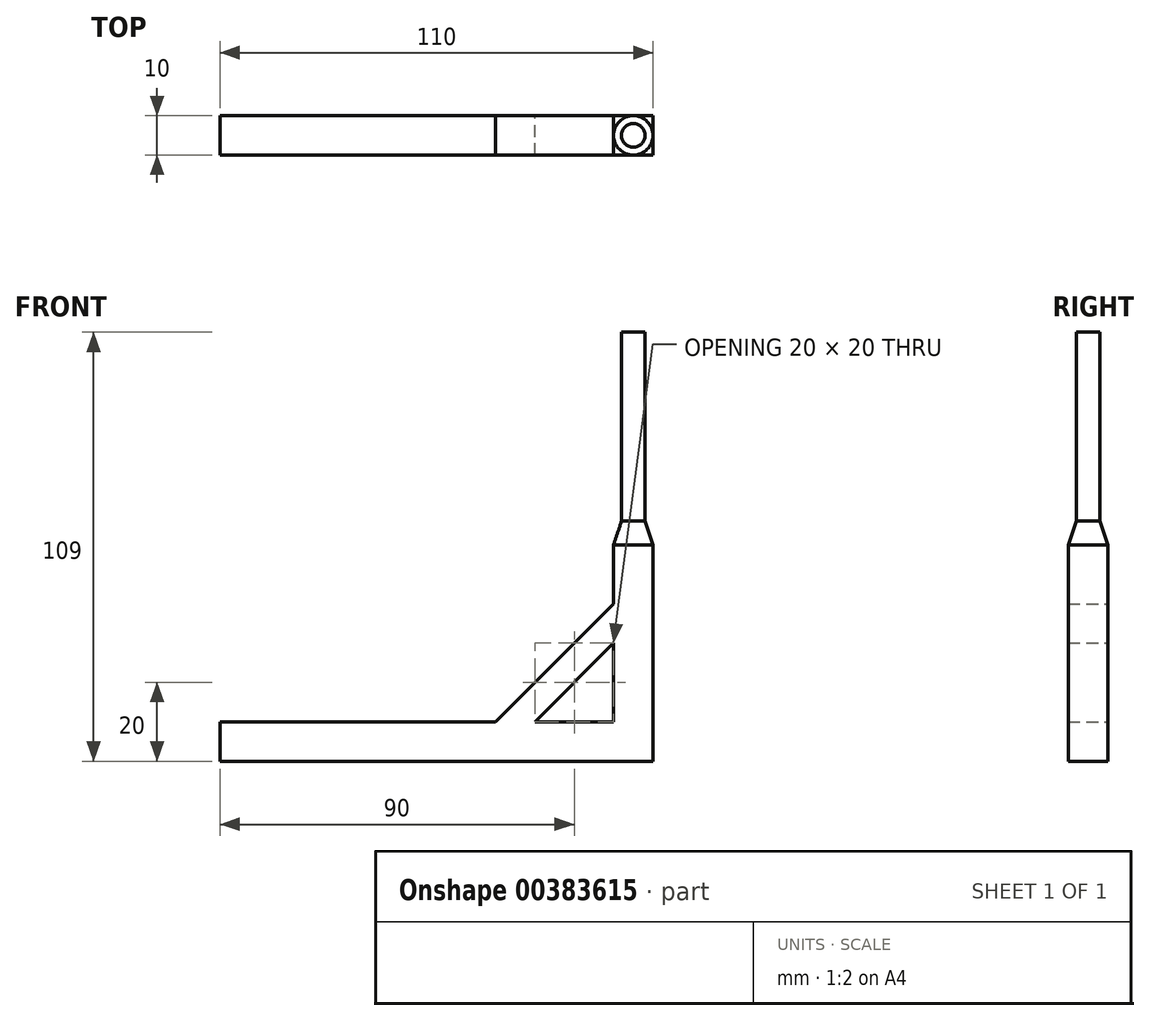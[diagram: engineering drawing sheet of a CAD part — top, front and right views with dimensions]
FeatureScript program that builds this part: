
annotation { "Feature Type Name" : "Feature", "Feature Type Description" : "" }
export const myFeature = defineFeature(function(context is Context, id is Id, definition is map)
    precondition{}
    {
        {
            var Q0;
            Q0=qCreatedBy(makeId("Top.planeOp"),FACE);
            var sketch = newSketch(context, id + "F0", { "sketchPlane" : qUnion([Q0])});
            skLineSegment(sketch, "E0.bottom", {"start": v(-55, 5) * mm, "end": v(55, 5) * mm});
            skLineSegment(sketch, "E0.top", {"start": v(-55, -5) * mm, "end": v(55, -5) * mm});
            skLineSegment(sketch, "E0.left", {"start": v(-55, 5) * mm, "end": v(-55, -5) * mm});
            skLineSegment(sketch, "E0.right", {"start": v(55, 5) * mm, "end": v(55, -5) * mm});
            skLineSegment(sketch, "E1", {"start": v(-55, 5) * mm, "end": v(55, -5) * mm, "construction": true});
            skLineSegment(sketch, "E2", {"start": v(55, 5) * mm, "end": v(-55, -5) * mm, "construction": true});
            skPoint(sketch, "E3", {"position": v(0, 0) * mm});
            skSolve(sketch);
        }
        {
            var Q0;
            Q0=makeQuery(id+"F0.imprint","IMPRINT",FACE,{"disambiguationData":[TD([[makeQuery(id+"F0.imprint","IMPRINT",EDGE,{"derivedFrom":sQuery(id+"F0.wireOp",EDGE,"E0.bottom")}),-1.0]])]});
            extrude(context, id + "F1", {"entities" : qUnion([Q0]), "depth" : 10 * mm});
        }
        {
            var Q0;
            Q0=makeQuery(id+"F1.opExtrude","CAP_FACE",FACE,{"disambiguationData":[OSD([sQuery(id+"F0.wireOp",EDGE,"E0.bottom"),sQuery(id+"F0.wireOp",EDGE,"E0.top"),sQuery(id+"F0.wireOp",EDGE,"E0.left"),sQuery(id+"F0.wireOp",EDGE,"E0.right")])],"isStart":false});
            var sketch = newSketch(context, id + "F2", { "sketchPlane" : qUnion([Q0])});
            skLineSegment(sketch, "E4.0", {"start": v(45, 5) * mm, "end": v(55, 5) * mm});
            skLineSegment(sketch, "E5.0", {"start": v(45, -5) * mm, "end": v(55, -5) * mm});
            skLineSegment(sketch, "E6.0", {"start": v(55, 5) * mm, "end": v(55, -5) * mm});
            skLineSegment(sketch, "E7", {"start": v(45, 5) * mm, "end": v(45, -5) * mm});
            skPoint(sketch, "E8.orphan", {"position": v(-55, 5) * mm});
            skPoint(sketch, "E9.orphan", {"position": v(-55, -5) * mm});
            skSolve(sketch);
        }
        {
            var Q0;
            Q0=makeQuery(id+"F2.imprint","IMPRINT",FACE,{"disambiguationData":[TD([[makeQuery(id+"F2.imprint","IMPRINT",EDGE,{"derivedFrom":sQuery(id+"F2.wireOp",EDGE,"E4.0")}),-1.0]])]});
            extrude(context, id + "F3", {"entities" : qUnion([Q0]), "operationType" : NewBodyOperationType.ADD, "depth" : 45 * mm});
        }
        {
            var Q0;
            Q0=makeQuery(id+"F3.opExtrude","CAP_FACE",FACE,{"disambiguationData":[OSD([sQuery(id+"F2.wireOp",EDGE,"E4.0"),sQuery(id+"F2.wireOp",EDGE,"E5.0"),sQuery(id+"F2.wireOp",EDGE,"E6.0"),sQuery(id+"F2.wireOp",EDGE,"E7")])],"isStart":false});
            var sketch = newSketch(context, id + "F4", { "sketchPlane" : qUnion([Q0])});
            skPoint(sketch, "E10.0", {"position": v(55, -5) * mm});
            skPoint(sketch, "E11.0", {"position": v(45, 5) * mm});
            skPoint(sketch, "E12.0", {"position": v(45, -5) * mm});
            skPoint(sketch, "E13.0", {"position": v(55, 5) * mm});
            skLineSegment(sketch, "E14", {"start": v(55, -5) * mm, "end": v(45, 5) * mm, "construction": true});
            skLineSegment(sketch, "E15", {"start": v(45, -5) * mm, "end": v(55, 5) * mm, "construction": true});
            skPoint(sketch, "E16", {"position": v(50, 0) * mm});
            skCircle(sketch, "E17", {"center": v(50, 0) * mm, "radius": 3 * mm});
            skSolve(sketch);
        }
        {
            var Q0;
            Q0 = qSketchRegion(id + "F4", true);
            extrude(context, id + "F5", {"entities" : qUnion([Q0]), "operationType" : NewBodyOperationType.ADD, "depth" : 54 * mm});
        }
        {
            var Q0;
            Q0=makeQuery(id+"F3.opExtrude","SWEPT_FACE",FACE,{"disambiguationData":[OSD([sQuery(id+"F2.wireOp",EDGE,"E7")])]});
            var Q1;
            Q1=makeQuery(id+"F3.boolean.opBoolean","MERGE",FACE,{"derivedFrom":[makeQuery(id+"F1.opExtrude","SWEPT_FACE",FACE,{"disambiguationData":[OSD([sQuery(id+"F0.wireOp",EDGE,"E0.right")])]}),makeQuery(id+"F3.opExtrude","SWEPT_FACE",FACE,{"disambiguationData":[OSD([sQuery(id+"F2.wireOp",EDGE,"E6.0")])]})]});
            cPlane(context, id + "F6", {"entities" : qUnion([Q0, Q1]), "cplaneType" : CPlaneType.MID_PLANE, "offset" : 25 * mm, "width" : 150 * mm, "height" : 150 * mm});
        }
        {
            var Q0;
            Q0=qCreatedBy(id+"F6.planeOp",FACE);
            var sketch = newSketch(context, id + "F7", { "sketchPlane" : qUnion([Q0])});
            skPoint(sketch, "E18.0", {"position": v(0, 55) * mm});
            skPoint(sketch, "E19.0", {"position": v(5, 55) * mm});
            skLineSegment(sketch, "E20", {"start": v(0, 55) * mm, "end": v(5, 55) * mm});
            skLineSegment(sketch, "E21", {"start": v(0, 55) * mm, "end": v(0, 70) * mm});
            skLineSegment(sketch, "E22", {"start": v(0, 70) * mm, "end": v(5, 55) * mm});
            skSolve(sketch);
        }
        {
            var Q0;
            Q0=qCreatedBy(id+"F6.planeOp",FACE);
            var sketch = newSketch(context, id + "F8", { "sketchPlane" : qUnion([Q0])});
            skLineSegment(sketch, "E23", {"start": v(0, 0) * mm, "end": v(0, 101.96) * mm});
            skSolve(sketch);
        }
        {
            var Q0;
            Q0=makeQuery(id+"F7.imprint","IMPRINT",FACE,{"disambiguationData":[TD([[makeQuery(id+"F7.imprint","IMPRINT",EDGE,{"derivedFrom":sQuery(id+"F7.wireOp",EDGE,"E20")}),1.0]])]});
            var Q1;
            Q1=sQuery(id+"F8.wireOp",EDGE,"E23");
            revolve(context, id + "F9", {"operationType" : NewBodyOperationType.ADD, "entities" : qUnion([Q0]), "axis" : qUnion([Q1]), "revolveType" : RevolveType.FULL});
        }
        {
            var Q0;
            Q0=makeQuery(id+"F3.boolean.opBoolean","MERGE",FACE,{"derivedFrom":[makeQuery(id+"F1.opExtrude","SWEPT_FACE",FACE,{"disambiguationData":[OSD([sQuery(id+"F0.wireOp",EDGE,"E0.bottom")])]}),makeQuery(id+"F3.opExtrude","SWEPT_FACE",FACE,{"disambiguationData":[OSD([sQuery(id+"F2.wireOp",EDGE,"E4.0")])]})]});
            cPlane(context, id + "F10", {"entities" : qUnion([Q0]), "cplaneType" : CPlaneType.OFFSET, "offset" : 0 * mm, "width" : 150 * mm, "height" : 150 * mm});
        }
        {
            var Q0;
            Q0=qCreatedBy(id+"F10.planeOp",FACE);
            var sketch = newSketch(context, id + "F11", { "sketchPlane" : qUnion([Q0])});
            skLineSegment(sketch, "E24.0", {"start": v(-15, 10) * mm, "end": v(-25, 10) * mm});
            skLineSegment(sketch, "E25", {"start": v(-45, 30) * mm, "end": v(-25, 10) * mm});
            skLineSegment(sketch, "E26", {"start": v(-45, 40) * mm, "end": v(-15, 10) * mm});
            skPoint(sketch, "E27.orphan", {"position": v(-45, 55) * mm});
            skPoint(sketch, "E28.orphan", {"position": v(55, 10) * mm});
            skPoint(sketch, "E29.orphan", {"position": v(-45, 10) * mm});
            skLineSegment(sketch, "E30.0", {"start": v(-45, 40) * mm, "end": v(-45, 10) * mm});
            skSolve(sketch);
        }
        {
            var Q0;
            Q0=makeQuery(id+"F11.imprint","IMPRINT",FACE,{"disambiguationData":[TD([[makeQuery(id+"F11.imprint","IMPRINT",EDGE,{"derivedFrom":sQuery(id+"F11.wireOp",EDGE,"E24.0")}),-1.0]])]});
            var Q1;
            Q1=makeQuery(id+"F3.boolean.opBoolean","MERGE",FACE,{"derivedFrom":[makeQuery(id+"F1.opExtrude","SWEPT_FACE",FACE,{"disambiguationData":[OSD([sQuery(id+"F0.wireOp",EDGE,"E0.top")])]}),makeQuery(id+"F3.opExtrude","SWEPT_FACE",FACE,{"disambiguationData":[OSD([sQuery(id+"F2.wireOp",EDGE,"E5.0")])]})]});
            extrude(context, id + "F12", {"entities" : qUnion([Q0]), "operationType" : NewBodyOperationType.ADD, "endBound" : BoundingType.UP_TO_SURFACE, "oppositeDirection" : true, "endBoundEntityFace" : qUnion([Q1]), "depth" : 25 * mm});
        }
    });
